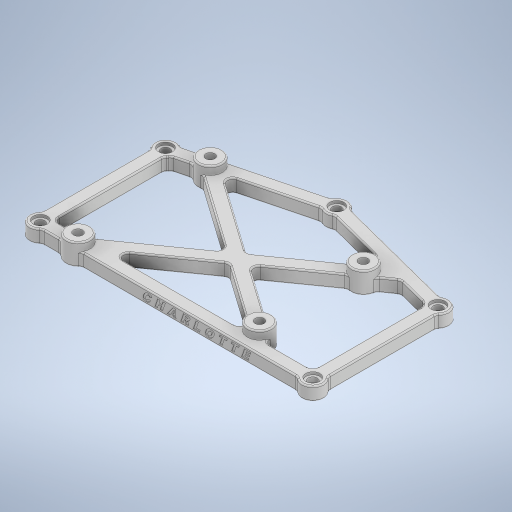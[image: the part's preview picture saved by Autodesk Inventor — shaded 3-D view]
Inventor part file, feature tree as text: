
AUTODESK INVENTOR PART (.ipt)
format: ipt  version: 2024.2 (Build 282272000, 272)  size: 1,252,864 bytes
history: native  units: mm
features: sketch x8, extrude x7, emboss x3, fillet x2, hole x1
ambient origin geometry x8: Origin, YZ Plane, XZ Plane, XY Plane, X Axis, Y Axis, Z Axis, Center Point
bodies: Solid1 (feature_tree)
feature tree (21):
  sketch  "Sketch1"  dims[d0=4.9mm d1=101.0mm]
  extrude  "Extrusion1"  Depth=4.9mm
  extrude  "Extrusion2"  Depth=50.5mm
  extrude  "Extrusion3"  Depth=8.0mm
  hole  "Hole1"  [1 undecoded]
  extrude  "Extrusion4"  Depth=62.0mm
  extrude  "Extrusion5"  Depth=5.0mm
  fillet  "Fillet1"  Radius=2.5mm
  fillet  "Fillet3"  Radius=5.0mm
  emboss  "Emboss1"
  emboss  "Emboss4"
  emboss  "Emboss5"
  extrude  "Extrusion6"  Depth=2.5mm
  extrude  "Extrusion7"  Depth=2.5mm
  sketch  "Sketch3"  dims[d2=13.0mm d3=50.5mm]
  sketch  "Sketch4"  dims[d4=8.0mm d6=49.0mm]
  sketch  "Sketch5"  dims[d7=46.4mm d8=5.25mm]
  sketch  "Sketch8"  dims[d9=5.25mm d10=62.0mm]
  sketch  "Sketch9"  dims[d12=9.0mm d13=5.0mm d14=2.5mm d21=5.0mm]
  sketch  "Sketch10"  dims[d22=2.5mm d23=2.5mm]
  sketch  "Sketch11"  dims[d30=5.0mm d31=2.5mm d32=2.5mm d33=5.0mm d35=2.5mm d38=3.4mm d39=5.0mm d40=2.5mm d41=2.5mm d42=5.0mm d43=5.0mm d44=2.5mm d45=2.5mm d46=2.5mm d47=2.5mm d48=5.0mm d49=0.0mm d52=8.0mm d53=0.0mm d54=1.9mm d55=0.0mm d56=3.4mm d57=6.0mm d58=4.0mm d59=2.0mm d60=90.0deg d61=8.0mm d62=20.594885mm d63=5.7mm d64=5.0mm d65=0.0mm d66=5.25mm d67=1.0mm d68=0.0mm d69=2.0mm d71=25.0mm d75=0.25mm d76=0.0mm d81=0.2mm d82=0.0mm d83=0.2mm d84=0.0mm d85=0.5mm d86=0.25mm d87=0.0mm d88=0.25mm d89=0.0mm]
note: 1 required parameter value undecoded (feature->parameter linkage not recoverable at this tier; creation-order binding heuristic only, values carry confidence <= 0.55)
